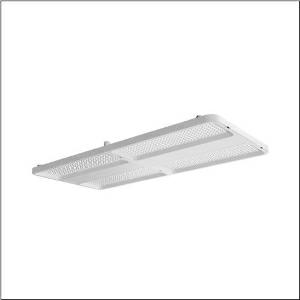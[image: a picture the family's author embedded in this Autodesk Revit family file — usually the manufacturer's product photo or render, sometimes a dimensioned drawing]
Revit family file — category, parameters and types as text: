
# Revit family: highbay_11_maxi_51hn12db4hda
name_source: partatom
category: Lighting Fixtures
units: mm (PartAtom-declared; Revit-internal decimal feet)

## family parameters
Cut with Voids When Loaded = No
Host = Face
Light Source = No
Part Type = Normal
Room Calculation Point = No
Round Connector Dimension = Use Diameter
Shared = No

## types (1)
- --- (1 x LED, 2990 lm, 15.1 W, 4000K)
    Apparent Load = 15 VA
    CIE Flux Codes = 87 98 100 100 100
    Color Rendering = 80
    Color Temperature = 4000K
    Default Elevation = 1800 mm
    Description = high bay luminaire Highbay 11 maxi; direct symmetric wide distribution, light control with lens of PMMA; UGR ≤ 19 (X = 4H | Y = 8H | S = 0.25H | reflection values 70/50/20); luminous flux: 20.000lm; light colour: 840, colour temperature: 4000K, MacAdam ≤ 2 SDCM (initial), colour rendering: CRI > 80; luminous efficacy: 210,7lm/W; rated service life: 100.000h (L95/B50) at AT= 25°C; control: DALI 2; luminaire connection: terminal, 5-pole, max. 2.5mm² (cable entry for one cable, Ø 8.5..16mm); mains connection: 230..240V, AC/DC 0/50..60Hz; connected load: 94,9W; protection rating (complete): IP66; insulation class (complete): insulation class I (protective earthing); protection symbol: D; impact resistance: IK08; certification: CE, ENEC, VDE, UKCA; luminaire for central battery installations according to DIN EN 60598-2-22, internal wiring halogen-free; luminaire corresponds to IFS (International Featured Standards) requirements for safety and quality in the food industry; LABS conformity tested according to VDMA 24364:2018-05; housing frame of high-performance plastic PA6, matt traffic white (RAL 9016); cover of PMMA; dimension (LxWxH): 946 x 442 x 72mm; permissible operating ambient temperature: -40..+65°C (reducing of maximum allowable ambient temperature of 5°C with ceiling mounting); packaging unit: 1 piece; (delivery without accessories; please order mounting accessories separately)
    Height = 72 mm  [stored 0.23622 ft]
    Lamp = 1 x LED
    Lamp Light Flux = 2990 lm
    Lamp Power = 15.1 W
    Lamp count = 1
    Length = 946 mm
    Luminous efficacy = 198 lm/W
    Manufacturer = Siteco
    ModVariant = No
    Model = 51HN12DB4HDA
    Mounting Place = Ceiling
    Mounting Type = Pendant
    Number of Poles = 1
    OnlyDefault = Yes
    Power Factor = 1
    Product Name = Highbay 11 maxi
    Product group = high bay luminaire
    ProductGroupID = 901
    Protection Class = Protection class I
    Protection Degree = IP 66
    RLX_Detail_Level = 1
    RLX_Emergency_Light_Flux = 0 lm
    RLX_Emergency_Type = 0
    RLX_Emergency_Type_DB = No
    RlxData = <blob elided: 127617 chars, md5=78a71825>
    Socket = socket
    Standby Power = 0 W
    System Light Flux = 2990 lm
    System Power = 15 W
    Type Comments = : DC mode (central or group accumulator) initial emergency light level
    Type Image = l_1363244.jpg
    URL = http://relux.com
    VarID = @adj_023443
    Voltage = 0 V
    Weight = 0.00 kg
    Width = 442 mm

note: [stored X ft] marks values corroborated as IEEE doubles in the binary element streams (Revit-internal decimal feet)

## geometry (parser evidence)
native form markers: Blend x4, Sweep x12
no freeform markers — native parametric forms only
